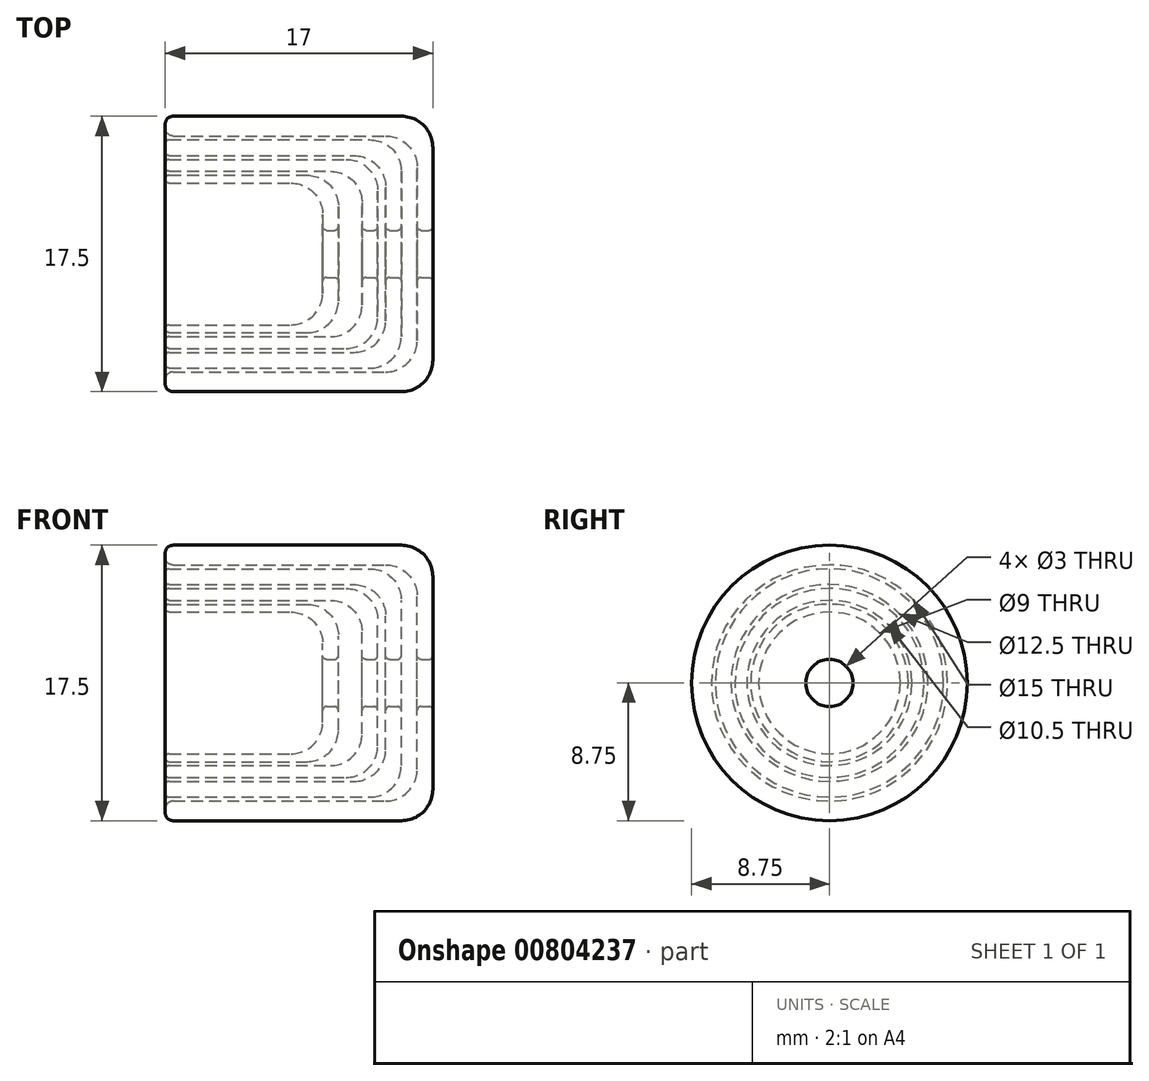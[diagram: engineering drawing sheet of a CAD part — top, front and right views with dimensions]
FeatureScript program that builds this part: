
annotation { "Feature Type Name" : "Feature", "Feature Type Description" : "" }
export const myFeature = defineFeature(function(context is Context, id is Id, definition is map)
    precondition{}
    {
        {
            var Q0;
            Q0=qCreatedBy(makeId("Front.planeOp"),FACE);
            var sketch = newSketch(context, id + "F0", { "sketchPlane" : qUnion([Q0])});
            skLineSegment(sketch, "E0", {"start": v(-4, 1.75) * mm, "end": v(-4, 6.75) * mm});
            skLineSegment(sketch, "E1", {"start": v(-6, 8.75) * mm, "end": v(-20.5, 8.75) * mm});
            skLineSegment(sketch, "E2", {"start": v(-20.5, 7.5) * mm, "end": v(-7, 7.5) * mm});
            skLineSegment(sketch, "E3", {"start": v(-5, 5.5) * mm, "end": v(-5, 1.75) * mm});
            skLineSegment(sketch, "E4", {"start": v(-4.75, 1.5) * mm, "end": v(-4.25, 1.5) * mm});
            skLineSegment(sketch, "E5", {"start": v(-6, 1.75) * mm, "end": v(-6, 5.25) * mm});
            skLineSegment(sketch, "E6", {"start": v(-8, 7.25) * mm, "end": v(-20.75, 7.25) * mm});
            skLineSegment(sketch, "E7", {"start": v(-20.75, 6.25) * mm, "end": v(-9, 6.25) * mm});
            skLineSegment(sketch, "E8", {"start": v(-7, 4.25) * mm, "end": v(-7, 1.75) * mm});
            skLineSegment(sketch, "E9", {"start": v(-6.75, 1.5) * mm, "end": v(-6.25, 1.5) * mm});
            skLineSegment(sketch, "E10", {"start": v(-7.5, 1.75) * mm, "end": v(-7.5, 4) * mm});
            skLineSegment(sketch, "E11", {"start": v(-9.5, 6) * mm, "end": v(-20.75, 6) * mm});
            skLineSegment(sketch, "E12", {"start": v(-20.75, 5.25) * mm, "end": v(-10.5, 5.25) * mm});
            skLineSegment(sketch, "E13", {"start": v(-8.5, 3.25) * mm, "end": v(-8.5, 1.75) * mm});
            skLineSegment(sketch, "E14", {"start": v(-8.25, 1.5) * mm, "end": v(-7.75, 1.5) * mm});
            skLineSegment(sketch, "E15", {"start": v(-10, 1.75) * mm, "end": v(-10, 3) * mm});
            skLineSegment(sketch, "E16", {"start": v(-12, 5) * mm, "end": v(-20.75, 5) * mm});
            skLineSegment(sketch, "E17", {"start": v(-20.75, 4.5) * mm, "end": v(-13, 4.5) * mm});
            skLineSegment(sketch, "E18", {"start": v(-11, 2.5) * mm, "end": v(-11, 1.75) * mm});
            skLineSegment(sketch, "E19", {"start": v(-10.75, 1.5) * mm, "end": v(-10.25, 1.5) * mm});
            skLineSegment(sketch, "E20", {"start": v(0, 0) * mm, "end": v(-10.3, 0) * mm});
            skLineSegment(sketch, "E21", {"start": v(-21, 8.25) * mm, "end": v(-21, 8) * mm});
            skLineSegment(sketch, "E22", {"start": v(-21, 7) * mm, "end": v(-21, 6.5) * mm});
            skLineSegment(sketch, "E23", {"start": v(-21, 5.75) * mm, "end": v(-21, 5.5) * mm});
            skLineSegment(sketch, "E24", {"start": v(-21, 4.75) * mm, "end": v(-21, 4.75) * mm});
            skPoint(sketch, "E25.visualSharp", {"position": v(-4, 8.75) * mm});
            skArc(sketch, "E25.filletArc", {"start": v(-4, 6.75) * mm, "mid": v(-4.59, 8.16) * mm, "end": v(-6, 8.75) * mm});
            skPoint(sketch, "E26.visualSharp", {"position": v(-5, 7.5) * mm});
            skArc(sketch, "E26.filletArc", {"start": v(-5, 5.5) * mm, "mid": v(-5.59, 6.91) * mm, "end": v(-7, 7.5) * mm});
            skPoint(sketch, "E27.visualSharp", {"position": v(-6, 7.25) * mm});
            skArc(sketch, "E27.filletArc", {"start": v(-6, 5.25) * mm, "mid": v(-6.59, 6.66) * mm, "end": v(-8, 7.25) * mm});
            skPoint(sketch, "E28.visualSharp", {"position": v(-7.5, 6) * mm});
            skArc(sketch, "E28.filletArc", {"start": v(-7.5, 4) * mm, "mid": v(-8.09, 5.41) * mm, "end": v(-9.5, 6) * mm});
            skPoint(sketch, "E29.visualSharp", {"position": v(-7, 6.25) * mm});
            skArc(sketch, "E29.filletArc", {"start": v(-7, 4.25) * mm, "mid": v(-7.59, 5.66) * mm, "end": v(-9, 6.25) * mm});
            skPoint(sketch, "E30.visualSharp", {"position": v(-8.5, 5.25) * mm});
            skArc(sketch, "E30.filletArc", {"start": v(-8.5, 3.25) * mm, "mid": v(-9.09, 4.66) * mm, "end": v(-10.5, 5.25) * mm});
            skPoint(sketch, "E31.visualSharp", {"position": v(-10, 5) * mm});
            skArc(sketch, "E31.filletArc", {"start": v(-10, 3) * mm, "mid": v(-10.59, 4.41) * mm, "end": v(-12, 5) * mm});
            skPoint(sketch, "E32.visualSharp", {"position": v(-11, 4.5) * mm});
            skArc(sketch, "E32.filletArc", {"start": v(-11, 2.5) * mm, "mid": v(-11.59, 3.91) * mm, "end": v(-13, 4.5) * mm});
            skPoint(sketch, "E33.visualSharp", {"position": v(-21, 8.75) * mm});
            skArc(sketch, "E33.filletArc", {"start": v(-20.5, 8.75) * mm, "mid": v(-20.85, 8.6) * mm, "end": v(-21, 8.25) * mm});
            skPoint(sketch, "E34.visualSharp", {"position": v(-21, 7.5) * mm});
            skArc(sketch, "E34.filletArc", {"start": v(-21, 8) * mm, "mid": v(-20.85, 7.65) * mm, "end": v(-20.5, 7.5) * mm});
            skPoint(sketch, "E35.visualSharp", {"position": v(-21, 7.25) * mm});
            skArc(sketch, "E35.filletArc", {"start": v(-20.75, 7.25) * mm, "mid": v(-20.93, 7.18) * mm, "end": v(-21, 7) * mm});
            skPoint(sketch, "E36.visualSharp", {"position": v(-21, 6.25) * mm});
            skArc(sketch, "E36.filletArc", {"start": v(-21, 6.5) * mm, "mid": v(-20.93, 6.32) * mm, "end": v(-20.75, 6.25) * mm});
            skPoint(sketch, "E37.visualSharp", {"position": v(-21, 6) * mm});
            skArc(sketch, "E37.filletArc", {"start": v(-20.75, 6) * mm, "mid": v(-20.93, 5.93) * mm, "end": v(-21, 5.75) * mm});
            skPoint(sketch, "E38.visualSharp", {"position": v(-21, 5.25) * mm});
            skArc(sketch, "E38.filletArc", {"start": v(-21, 5.5) * mm, "mid": v(-20.93, 5.32) * mm, "end": v(-20.75, 5.25) * mm});
            skPoint(sketch, "E39.visualSharp", {"position": v(-21, 5) * mm});
            skArc(sketch, "E39.filletArc", {"start": v(-20.75, 5) * mm, "mid": v(-20.93, 4.93) * mm, "end": v(-21, 4.75) * mm});
            skPoint(sketch, "E40.visualSharp", {"position": v(-21, 4.5) * mm});
            skArc(sketch, "E40.filletArc", {"start": v(-21, 4.75) * mm, "mid": v(-20.93, 4.57) * mm, "end": v(-20.75, 4.5) * mm});
            skPoint(sketch, "E41.visualSharp", {"position": v(-11, 1.5) * mm});
            skArc(sketch, "E41.filletArc", {"start": v(-11, 1.75) * mm, "mid": v(-10.93, 1.57) * mm, "end": v(-10.75, 1.5) * mm});
            skPoint(sketch, "E42.visualSharp", {"position": v(-10, 1.5) * mm});
            skArc(sketch, "E42.filletArc", {"start": v(-10.25, 1.5) * mm, "mid": v(-10.07, 1.57) * mm, "end": v(-10, 1.75) * mm});
            skPoint(sketch, "E43.visualSharp", {"position": v(-8.5, 1.5) * mm});
            skArc(sketch, "E43.filletArc", {"start": v(-8.5, 1.75) * mm, "mid": v(-8.43, 1.57) * mm, "end": v(-8.25, 1.5) * mm});
            skPoint(sketch, "E44.visualSharp", {"position": v(-7.5, 1.5) * mm});
            skArc(sketch, "E44.filletArc", {"start": v(-7.75, 1.5) * mm, "mid": v(-7.57, 1.57) * mm, "end": v(-7.5, 1.75) * mm});
            skPoint(sketch, "E45.visualSharp", {"position": v(-7, 1.5) * mm});
            skArc(sketch, "E45.filletArc", {"start": v(-7, 1.75) * mm, "mid": v(-6.93, 1.57) * mm, "end": v(-6.75, 1.5) * mm});
            skPoint(sketch, "E46.visualSharp", {"position": v(-6, 1.5) * mm});
            skArc(sketch, "E46.filletArc", {"start": v(-6.25, 1.5) * mm, "mid": v(-6.07, 1.57) * mm, "end": v(-6, 1.75) * mm});
            skPoint(sketch, "E47.visualSharp", {"position": v(-5, 1.5) * mm});
            skArc(sketch, "E47.filletArc", {"start": v(-5, 1.75) * mm, "mid": v(-4.93, 1.57) * mm, "end": v(-4.75, 1.5) * mm});
            skPoint(sketch, "E48.visualSharp", {"position": v(-4, 1.5) * mm});
            skArc(sketch, "E48.filletArc", {"start": v(-4.25, 1.5) * mm, "mid": v(-4.07, 1.57) * mm, "end": v(-4, 1.75) * mm});
            skSolve(sketch);
        }
        {
            var Q0;
            Q0 = qSketchRegion(id + "F0", true);
            var Q1;
            Q1=sQuery(id+"F0.wireOp",EDGE,"E20");
            revolve(context, id + "F1", {"surfaceOperationType" : NewSurfaceOperationType.NEW, "entities" : qUnion([Q0]), "axis" : qUnion([Q1]), "revolveType" : RevolveType.FULL});
        }
    });
